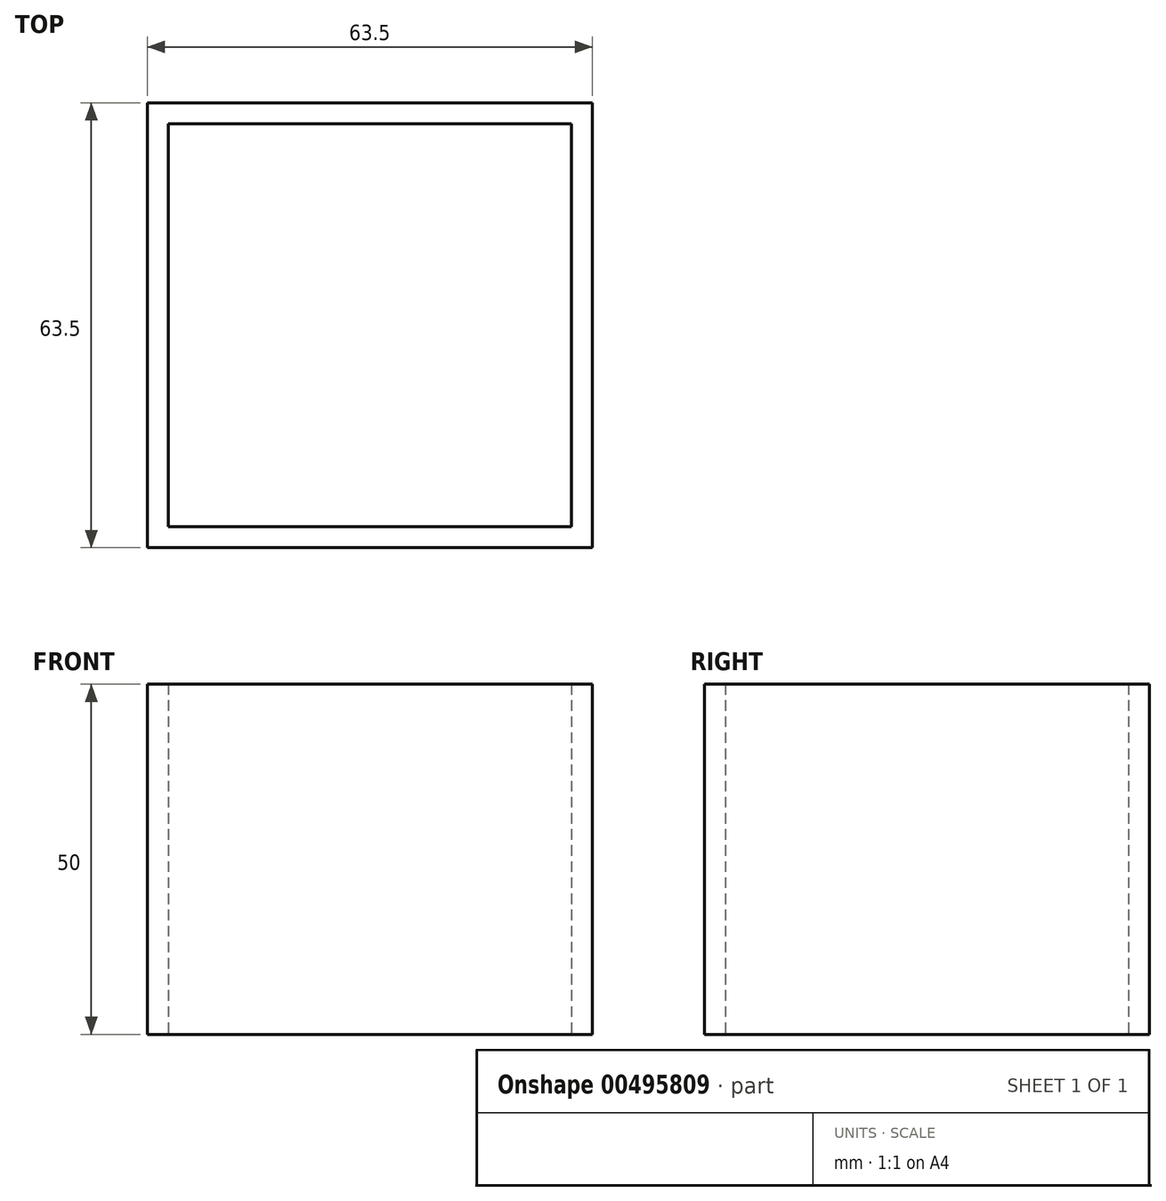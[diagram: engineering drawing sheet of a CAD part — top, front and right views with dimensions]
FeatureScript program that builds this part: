
annotation { "Feature Type Name" : "Feature", "Feature Type Description" : "" }
export const myFeature = defineFeature(function(context is Context, id is Id, definition is map)
    precondition{}
    {
        {
            var Q0;
            Q0=qCreatedBy(makeId("Top.planeOp"),FACE);
            var sketch = newSketch(context, id + "F0", { "sketchPlane" : qUnion([Q0])});
            skLineSegment(sketch, "E0.bottom", {"start": v(-27.29, 27.59) * mm, "end": v(36.21, 27.59) * mm});
            skLineSegment(sketch, "E0.top", {"start": v(-27.29, -35.91) * mm, "end": v(36.21, -35.91) * mm});
            skLineSegment(sketch, "E0.left", {"start": v(-27.29, 27.59) * mm, "end": v(-27.29, -35.91) * mm});
            skLineSegment(sketch, "E0.right", {"start": v(36.21, 27.59) * mm, "end": v(36.21, -35.91) * mm});
            skLineSegment(sketch, "E1.bottom", {"start": v(-24.29, 24.59) * mm, "end": v(33.21, 24.59) * mm});
            skLineSegment(sketch, "E1.top", {"start": v(-24.29, -32.91) * mm, "end": v(33.21, -32.91) * mm});
            skLineSegment(sketch, "E1.left", {"start": v(-24.29, 24.59) * mm, "end": v(-24.29, -32.91) * mm});
            skLineSegment(sketch, "E1.right", {"start": v(33.21, 24.59) * mm, "end": v(33.21, -32.91) * mm});
            skSolve(sketch);
        }
        {
            var Q0;
            Q0 = qSketchRegion(id + "F0", true);
            extrude(context, id + "F1", {"entities" : qUnion([Q0]), "depth" : 50 * mm});
        }
    });
